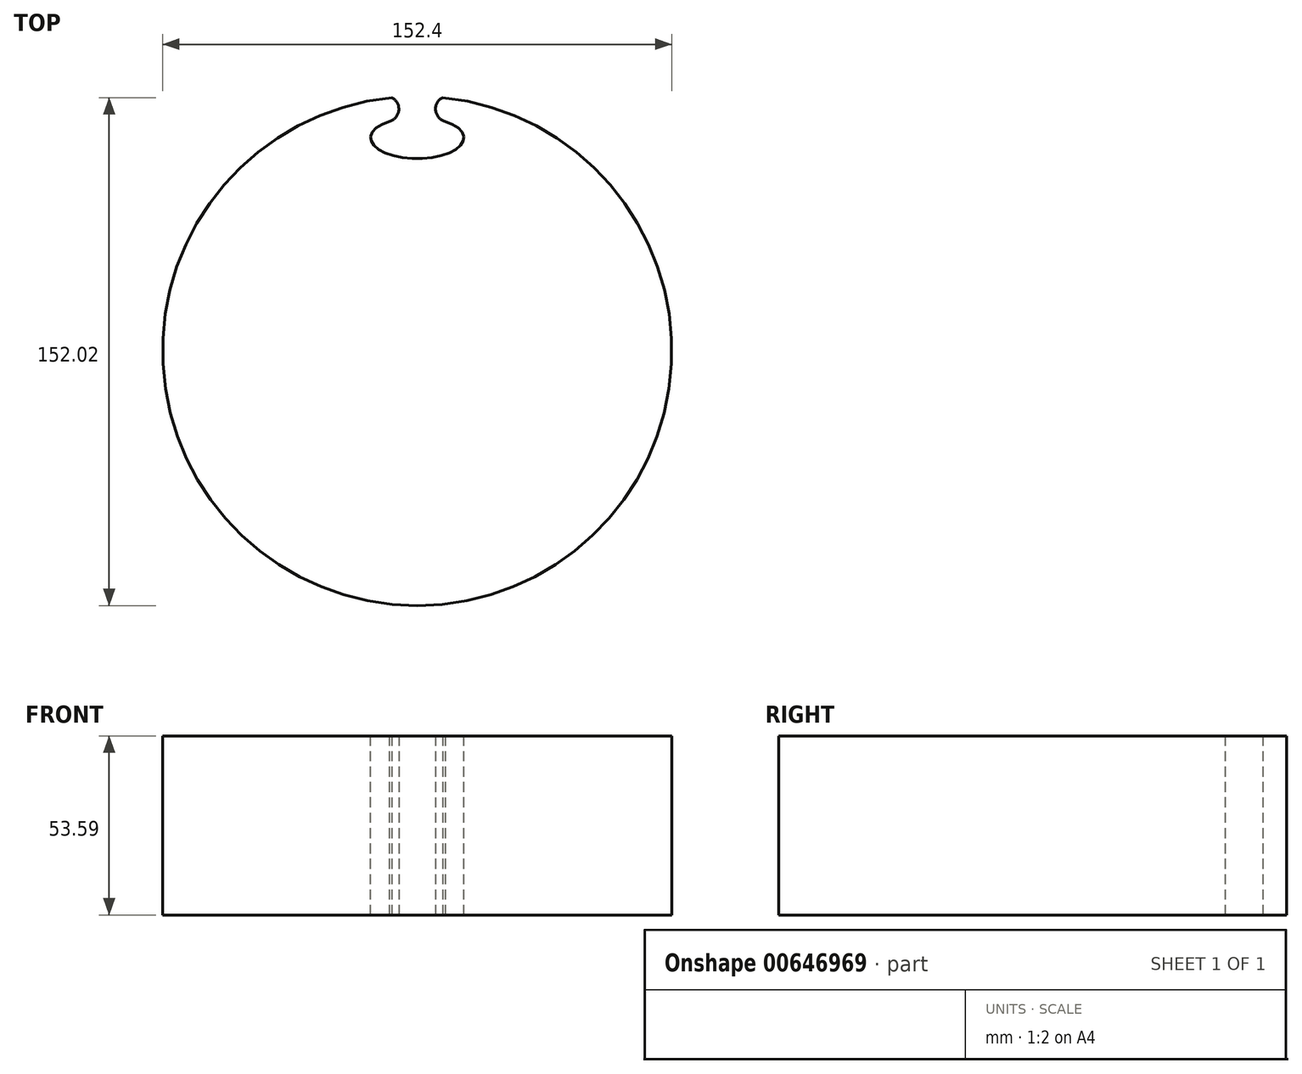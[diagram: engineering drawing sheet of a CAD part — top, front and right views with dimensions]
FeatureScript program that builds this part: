
annotation { "Feature Type Name" : "Feature", "Feature Type Description" : "" }
export const myFeature = defineFeature(function(context is Context, id is Id, definition is map)
    precondition{}
    {
        {
            var Q0;
            Q0=qCreatedBy(makeId("Top.planeOp"),FACE);
            var sketch = newSketch(context, id + "F0", { "sketchPlane" : qUnion([Q0])});
            skArc(sketch, "E0", {"start": v(-7.62, 75.82) * mm, "mid": v(0, -76.2) * mm, "end": v(7.62, 75.82) * mm});
            skArc(sketch, "E1", {"start": v(-8.33, 68.71) * mm, "mid": v(-5.5, 72.02) * mm, "end": v(-7.62, 75.82) * mm});
            skArc(sketch, "E2", {"start": v(7.62, 75.82) * mm, "mid": v(5.5, 72.02) * mm, "end": v(8.33, 68.71) * mm});
            skEllipticalArc(sketch, "E3", {});
            const initialGuessF0  = {"E3": [0, 0.06375255435705185, 1, 0, 0.013940693025789356, 0.006187257356756456, 2.2115019328807275, 0.9300907207008382]};
            skSetInitialGuess(sketch, initialGuessF0);
            skSolve(sketch);
        }
        {
            var Q0;
            Q0=makeQuery(id+"F0.imprint","IMPRINT",FACE,{"disambiguationData":[TD([[makeQuery(id+"F0.imprint","IMPRINT",EDGE,{"derivedFrom":sQuery(id+"F0.wireOp",EDGE,"E0")}),1.0]])]});
            extrude(context, id + "F1", {"entities" : qUnion([Q0]), "depth" : 53.6 * mm, "offsetDistance" : 25.4 * mm});
        }
    });
